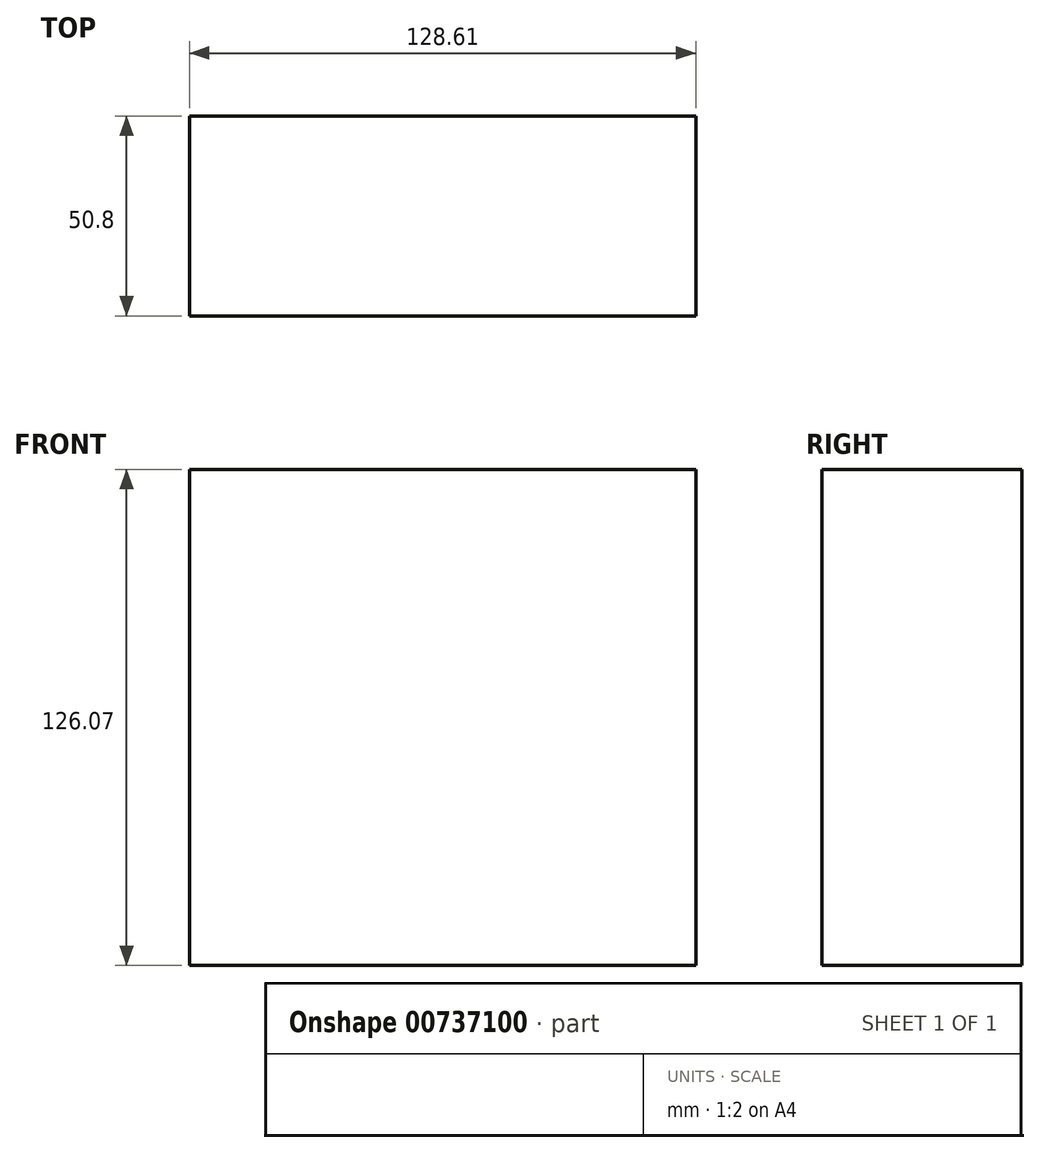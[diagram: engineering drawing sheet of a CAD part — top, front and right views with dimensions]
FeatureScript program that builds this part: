
annotation { "Feature Type Name" : "Feature", "Feature Type Description" : "" }
export const myFeature = defineFeature(function(context is Context, id is Id, definition is map)
    precondition{}
    {
        {
            var Q0;
            Q0=qCreatedBy(makeId("Front.planeOp"),FACE);
            var sketch = newSketch(context, id + "F0", { "sketchPlane" : qUnion([Q0])});
            skLineSegment(sketch, "E0.bottom", {"start": v(-67.84, 65.3) * mm, "end": v(60.77, 65.3) * mm});
            skLineSegment(sketch, "E0.top", {"start": v(-67.84, -60.76) * mm, "end": v(60.77, -60.76) * mm});
            skLineSegment(sketch, "E0.left", {"start": v(-67.84, 65.3) * mm, "end": v(-67.84, -60.76) * mm});
            skLineSegment(sketch, "E0.right", {"start": v(60.77, 65.3) * mm, "end": v(60.77, -60.76) * mm});
            skSolve(sketch);
        }
        {
            var Q0;
            Q0=makeQuery(id+"F0.imprint","IMPRINT",FACE,{"disambiguationData":[TD([[makeQuery(id+"F0.imprint","IMPRINT",EDGE,{"derivedFrom":sQuery(id+"F0.wireOp",EDGE,"E0.bottom")}),-1.0]])]});
            extrude(context, id + "F1", {"entities" : qUnion([Q0]), "depth" : 50.8 * mm, "offsetDistance" : 25.4 * mm});
        }
    });
